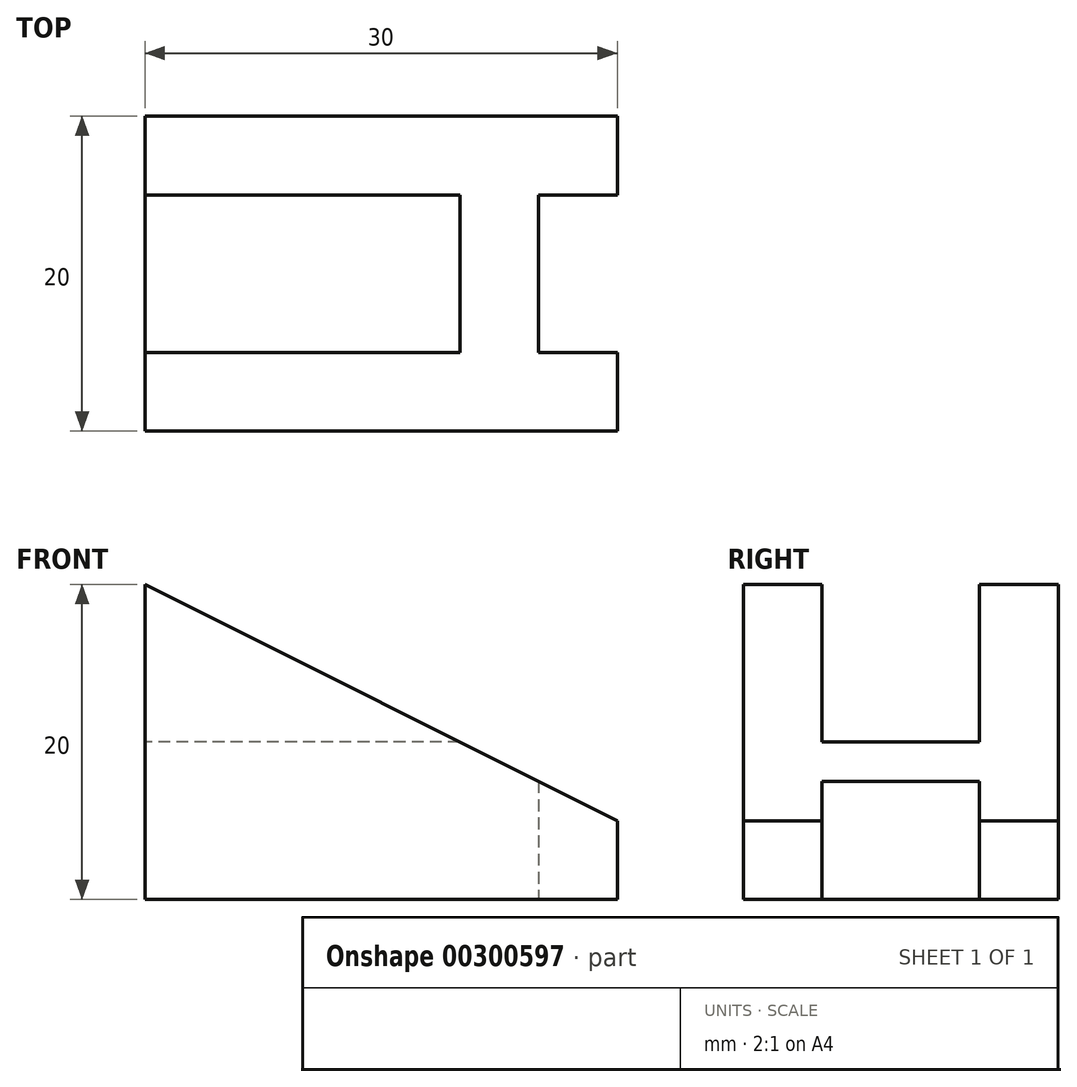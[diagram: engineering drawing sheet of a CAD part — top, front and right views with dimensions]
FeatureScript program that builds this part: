
annotation { "Feature Type Name" : "Feature", "Feature Type Description" : "" }
export const myFeature = defineFeature(function(context is Context, id is Id, definition is map)
    precondition{}
    {
        {
            var Q0;
            Q0=qCreatedBy(makeId("Front.planeOp"),FACE);
            var sketch = newSketch(context, id + "F0", { "sketchPlane" : qUnion([Q0])});
            skLineSegment(sketch, "E0", {"start": v(0, 0) * mm, "end": v(0, 20) * mm});
            skLineSegment(sketch, "E1", {"start": v(0, 20) * mm, "end": v(30, 5) * mm});
            skLineSegment(sketch, "E2", {"start": v(30, 5) * mm, "end": v(30, 0) * mm});
            skLineSegment(sketch, "E3", {"start": v(30, 0) * mm, "end": v(0, 0) * mm});
            skSolve(sketch);
        }
        {
            var Q0;
            Q0 = qSketchRegion(id + "F0", true);
            extrude(context, id + "F1", {"entities" : qUnion([Q0]), "endBound" : BoundingType.SYMMETRIC, "depth" : 20 * mm});
        }
        {
            var Q0;
            Q0=qCreatedBy(makeId("Top.planeOp"),FACE);
            var sketch = newSketch(context, id + "F2", { "sketchPlane" : qUnion([Q0])});
            skLineSegment(sketch, "E4", {"start": v(33.03, 0) * mm, "end": v(10.63, 0) * mm, "construction": true});
            skLineSegment(sketch, "E5", {"start": v(30, 0) * mm, "end": v(30, 5) * mm});
            skLineSegment(sketch, "E6", {"start": v(30, 5) * mm, "end": v(25, 5) * mm});
            skLineSegment(sketch, "E7", {"start": v(25, 5) * mm, "end": v(25, 0) * mm});
            skLineSegment(sketch, "E8.MirrorCS", {"start": v(30, 0) * mm, "end": v(30, -5) * mm});
            skLineSegment(sketch, "E9.MirrorCS", {"start": v(30, -5) * mm, "end": v(25, -5) * mm});
            skLineSegment(sketch, "E10.MirrorCS", {"start": v(25, -5) * mm, "end": v(25, 0) * mm});
            skSolve(sketch);
        }
        {
            var Q0;
            Q0 = qSketchRegion(id + "F2", true);
            extrude(context, id + "F3", {"entities" : qUnion([Q0]), "operationType" : NewBodyOperationType.REMOVE, "endBound" : BoundingType.THROUGH_ALL, "depth" : 25 * mm});
        }
        {
            var Q0;
            Q0=qCreatedBy(makeId("Right.planeOp"),FACE);
            var sketch = newSketch(context, id + "F4", { "sketchPlane" : qUnion([Q0])});
            skLineSegment(sketch, "E11", {"start": v(0, 24.58) * mm, "end": v(0, -3.48) * mm, "construction": true});
            skLineSegment(sketch, "E12", {"start": v(5, 20) * mm, "end": v(5, 10) * mm});
            skLineSegment(sketch, "E13", {"start": v(5, 10) * mm, "end": v(0, 10) * mm});
            skLineSegment(sketch, "E14", {"start": v(5, 20) * mm, "end": v(0, 20) * mm});
            skLineSegment(sketch, "E15.MirrorCS", {"start": v(-5, 20) * mm, "end": v(0, 20) * mm});
            skLineSegment(sketch, "E16.MirrorCS", {"start": v(-5, 20) * mm, "end": v(-5, 10) * mm});
            skLineSegment(sketch, "E17.MirrorCS", {"start": v(-5, 10) * mm, "end": v(0, 10) * mm});
            skSolve(sketch);
        }
        {
            var Q0;
            Q0=makeQuery(id+"F4.imprint","IMPRINT",FACE,{"disambiguationData":[TD([[makeQuery(id+"F4.imprint","IMPRINT",EDGE,{"derivedFrom":sQuery(id+"F4.wireOp",EDGE,"E12")}),-1.0]])]});
            extrude(context, id + "F5", {"entities" : qUnion([Q0]), "operationType" : NewBodyOperationType.REMOVE, "depth" : 20 * mm});
        }
    });
